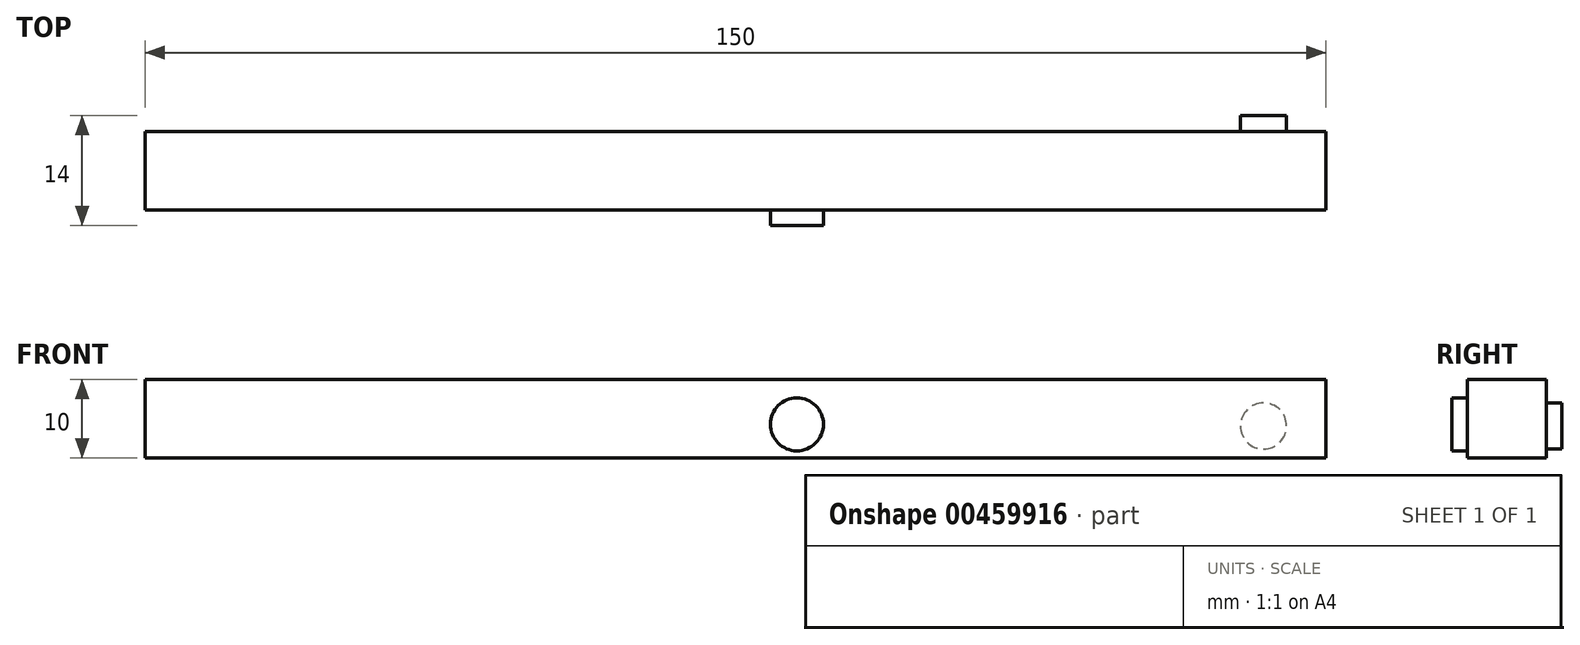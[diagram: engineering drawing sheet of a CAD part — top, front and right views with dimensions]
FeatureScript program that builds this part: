
annotation { "Feature Type Name" : "Feature", "Feature Type Description" : "" }
export const myFeature = defineFeature(function(context is Context, id is Id, definition is map)
    precondition{}
    {
        {
            var Q0;
            Q0=qCreatedBy(makeId("Front.planeOp"),FACE);
            var sketch = newSketch(context, id + "F0", { "sketchPlane" : qUnion([Q0])});
            skLineSegment(sketch, "E0.bottom", {"start": v(-75.95, 10.63) * mm, "end": v(74.05, 10.63) * mm});
            skLineSegment(sketch, "E0.top", {"start": v(-75.95, 0.63) * mm, "end": v(74.05, 0.63) * mm});
            skLineSegment(sketch, "E0.left", {"start": v(-75.95, 10.63) * mm, "end": v(-75.95, 0.63) * mm});
            skLineSegment(sketch, "E0.right", {"start": v(74.05, 10.63) * mm, "end": v(74.05, 0.63) * mm});
            skSolve(sketch);
        }
        {
            var Q0;
            Q0=makeQuery(id+"F0.imprint","IMPRINT",FACE,{"disambiguationData":[TD([[makeQuery(id+"F0.imprint","IMPRINT",EDGE,{"derivedFrom":sQuery(id+"F0.wireOp",EDGE,"E0.bottom")}),-1.0]])]});
            extrude(context, id + "F1", {"entities" : qUnion([Q0]), "depth" : 10 * mm});
        }
        {
            var Q0;
            Q0=makeQuery(id+"F1.opExtrude","CAP_FACE",FACE,{"disambiguationData":[OSD([sQuery(id+"F0.wireOp",EDGE,"E0.bottom"),sQuery(id+"F0.wireOp",EDGE,"E0.top"),sQuery(id+"F0.wireOp",EDGE,"E0.left"),sQuery(id+"F0.wireOp",EDGE,"E0.right")])],"isStart":true});
            var sketch = newSketch(context, id + "F2", { "sketchPlane" : qUnion([Q0])});
            skCircle(sketch, "E1", {"center": v(-66.12, 4.7) * mm, "radius": 2.93 * mm});
            skSolve(sketch);
        }
        {
            var Q0;
            Q0=makeQuery(id+"F1.opExtrude","CAP_FACE",FACE,{"disambiguationData":[OSD([sQuery(id+"F0.wireOp",EDGE,"E0.bottom"),sQuery(id+"F0.wireOp",EDGE,"E0.top"),sQuery(id+"F0.wireOp",EDGE,"E0.left"),sQuery(id+"F0.wireOp",EDGE,"E0.right")])],"isStart":false});
            var sketch = newSketch(context, id + "F3", { "sketchPlane" : qUnion([Q0])});
            skCircle(sketch, "E2", {"center": v(6.85, 4.9) * mm, "radius": 3.37 * mm});
            skSolve(sketch);
        }
        {
            var Q0;
            Q0=makeQuery(id+"F3.imprint","IMPRINT",FACE,{"disambiguationData":[TD([[makeQuery(id+"F3.imprint","IMPRINT",EDGE,{"derivedFrom":sQuery(id+"F3.wireOp",EDGE,"E2")}),1.0]])]});
            extrude(context, id + "F4", {"entities" : qUnion([Q0]), "operationType" : NewBodyOperationType.ADD, "depth" : 2 * mm});
        }
        {
            var Q0;
            Q0=makeQuery(id+"F2.imprint","IMPRINT",FACE,{"disambiguationData":[TD([[makeQuery(id+"F2.imprint","IMPRINT",EDGE,{"derivedFrom":sQuery(id+"F2.wireOp",EDGE,"E1")}),1.0]])]});
            extrude(context, id + "F5", {"entities" : qUnion([Q0]), "operationType" : NewBodyOperationType.ADD, "depth" : 2 * mm});
        }
    });
